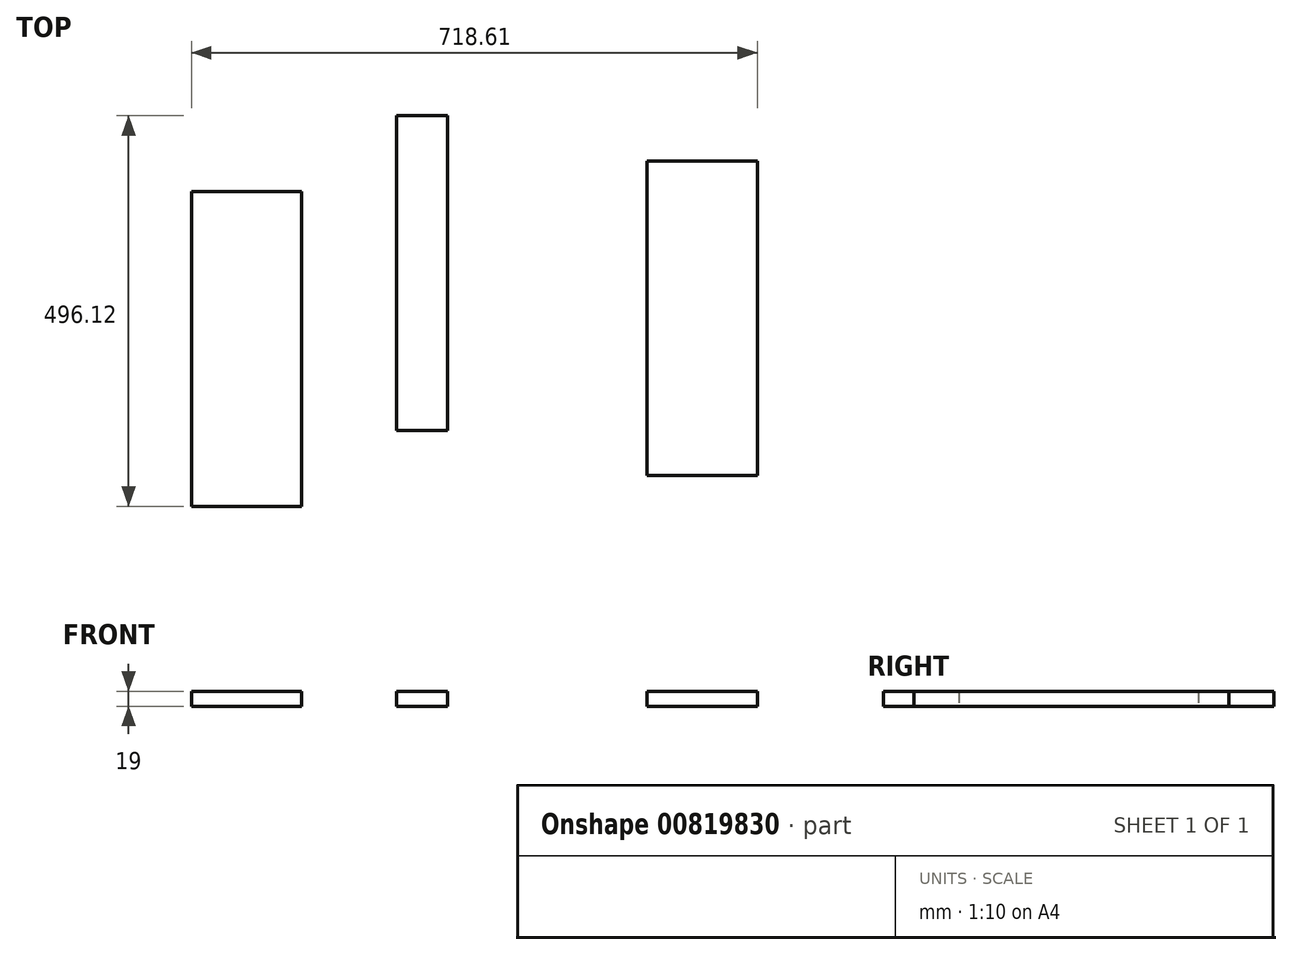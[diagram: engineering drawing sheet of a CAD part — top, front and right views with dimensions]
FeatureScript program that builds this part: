
annotation { "Feature Type Name" : "Feature", "Feature Type Description" : "" }
export const myFeature = defineFeature(function(context is Context, id is Id, definition is map)
    precondition{}
    {
        {
            var Q0;
            Q0=qCreatedBy(makeId("Top.planeOp"),FACE);
            var sketch = newSketch(context, id + "F0", { "sketchPlane" : qUnion([Q0])});
            skLineSegment(sketch, "E0.bottom", {"start": v(-5.44, -195.76) * mm, "end": v(-145.44, -195.76) * mm});
            skLineSegment(sketch, "E0.top", {"start": v(-5.44, 204.24) * mm, "end": v(-145.44, 204.24) * mm});
            skLineSegment(sketch, "E0.left", {"start": v(-5.44, -195.76) * mm, "end": v(-5.44, 204.24) * mm});
            skLineSegment(sketch, "E0.right", {"start": v(-145.44, -195.76) * mm, "end": v(-145.44, 204.24) * mm});
            skSolve(sketch);
        }
        {
            var Q0;
            Q0 = qSketchRegion(id + "F0", true);
            extrude(context, id + "F1", {"entities" : qUnion([Q0]), "depth" : 19 * mm, "offsetDistance" : 25 * mm});
        }
        {
            var Q0;
            Q0=qCreatedBy(makeId("Top.planeOp"),FACE);
            var sketch = newSketch(context, id + "F2", { "sketchPlane" : qUnion([Q0])});
            skLineSegment(sketch, "E1.bottom", {"start": v(433.17, -156.97) * mm, "end": v(573.17, -156.97) * mm});
            skLineSegment(sketch, "E1.top", {"start": v(433.17, 243.03) * mm, "end": v(573.17, 243.03) * mm});
            skLineSegment(sketch, "E1.left", {"start": v(433.17, -156.97) * mm, "end": v(433.17, 243.03) * mm});
            skLineSegment(sketch, "E1.right", {"start": v(573.17, -156.97) * mm, "end": v(573.17, 243.03) * mm});
            skSolve(sketch);
        }
        {
            var Q0;
            Q0 = qSketchRegion(id + "F2", true);
            extrude(context, id + "F3", {"entities" : qUnion([Q0]), "depth" : 19 * mm, "offsetDistance" : 25 * mm});
        }
        {
            var Q0;
            Q0=qCreatedBy(makeId("Top.planeOp"),FACE);
            var sketch = newSketch(context, id + "F4", { "sketchPlane" : qUnion([Q0])});
            skLineSegment(sketch, "E2.bottom", {"start": v(114.6, 300.36) * mm, "end": v(179.6, 300.36) * mm});
            skLineSegment(sketch, "E2.top", {"start": v(114.6, -99.64) * mm, "end": v(179.6, -99.64) * mm});
            skLineSegment(sketch, "E2.left", {"start": v(114.6, 300.36) * mm, "end": v(114.6, -99.64) * mm});
            skLineSegment(sketch, "E2.right", {"start": v(179.6, 300.36) * mm, "end": v(179.6, -99.64) * mm});
            skSolve(sketch);
        }
        {
            var Q0;
            Q0 = qSketchRegion(id + "F4", true);
            extrude(context, id + "F5", {"entities" : qUnion([Q0]), "depth" : 19 * mm, "offsetDistance" : 25 * mm});
        }
    });
